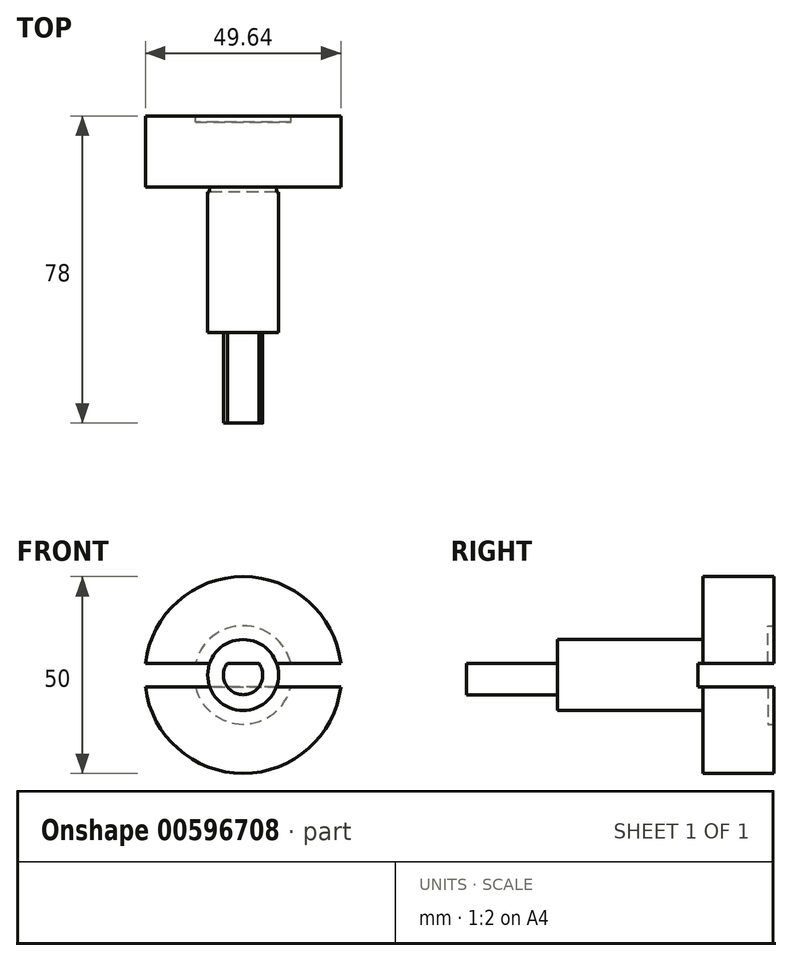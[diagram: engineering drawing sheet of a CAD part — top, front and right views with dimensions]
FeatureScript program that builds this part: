
annotation { "Feature Type Name" : "Feature", "Feature Type Description" : "" }
export const myFeature = defineFeature(function(context is Context, id is Id, definition is map)
    precondition{}
    {
        {
            var Q0;
            Q0=qCreatedBy(makeId("Right.planeOp"),FACE);
            var sketch = newSketch(context, id + "F0", { "sketchPlane" : qUnion([Q0])});
            skLineSegment(sketch, "E0", {"start": v(30.94, 0) * mm, "end": v(-47.06, 0) * mm});
            skLineSegment(sketch, "E1", {"start": v(-47.06, 0) * mm, "end": v(-47.06, -5) * mm});
            skLineSegment(sketch, "E2", {"start": v(-47.06, -5) * mm, "end": v(-24.06, -5) * mm});
            skLineSegment(sketch, "E3", {"start": v(-24.06, -5) * mm, "end": v(-24.06, -9) * mm});
            skLineSegment(sketch, "E4", {"start": v(-24.06, -9) * mm, "end": v(12.94, -9) * mm});
            skLineSegment(sketch, "E5", {"start": v(12.94, -9) * mm, "end": v(12.94, -25) * mm});
            skLineSegment(sketch, "E6", {"start": v(12.94, -25) * mm, "end": v(30.94, -25) * mm});
            skLineSegment(sketch, "E7", {"start": v(30.94, -25) * mm, "end": v(30.94, 0) * mm});
            skPoint(sketch, "E8.orphan", {"position": v(42.43, 0) * mm});
            skSolve(sketch);
        }
        {
            var Q0;
            Q0=makeQuery(id+"F0.imprint","IMPRINT",FACE,{"disambiguationData":[TD([[makeQuery(id+"F0.imprint","IMPRINT",EDGE,{"derivedFrom":sQuery(id+"F0.wireOp",EDGE,"E0")}),1.0]])]});
            var Q1;
            Q1=sQuery(id+"F0.wireOp",EDGE,"E0");
            revolve(context, id + "F1", {"entities" : qUnion([Q0]), "axis" : qUnion([Q1]), "revolveType" : RevolveType.FULL});
        }
        {
            var Q0;
            Q0=makeQuery(id+"F1.opRevolve","SWEPT_FACE",FACE,{"disambiguationData":[OSD([sQuery(id+"F0.wireOp",EDGE,"E1")])]});
            var sketch = newSketch(context, id + "F2", { "sketchPlane" : qUnion([Q0])});
            skLineSegment(sketch, "E9.bottom", {"start": v(-16.56, 13.75) * mm, "end": v(16.21, 13.75) * mm});
            skLineSegment(sketch, "E9.top", {"start": v(-16.56, 3) * mm, "end": v(16.21, 3) * mm});
            skLineSegment(sketch, "E9.left", {"start": v(-16.56, 13.75) * mm, "end": v(-16.56, 3) * mm});
            skLineSegment(sketch, "E9.right", {"start": v(16.21, 13.75) * mm, "end": v(16.21, 3) * mm});
            skSolve(sketch);
        }
        {
            var Q0;
            Q0 = qSketchRegion(id + "F2", true);
            var Q1;
            Q1=makeQuery(id+"F1.opRevolve","SWEPT_FACE",FACE,{"disambiguationData":[OSD([sQuery(id+"F0.wireOp",EDGE,"E3")])]});
            extrude(context, id + "F3", {"entities" : qUnion([Q0]), "operationType" : NewBodyOperationType.REMOVE, "endBound" : BoundingType.UP_TO_SURFACE, "oppositeDirection" : true, "depth" : 25 * mm, "endBoundEntityFace" : qUnion([Q1]), "offsetDistance" : 25 * mm});
        }
        {
            var Q0;
            Q0=makeQuery(id+"F1.opRevolve","SWEPT_FACE",FACE,{"disambiguationData":[OSD([sQuery(id+"F0.wireOp",EDGE,"E7")])]});
            var sketch = newSketch(context, id + "F4", { "sketchPlane" : qUnion([Q0])});
            skLineSegment(sketch, "E10.bottom", {"start": v(-27.5, 3) * mm, "end": v(27.5, 3) * mm});
            skLineSegment(sketch, "E10.top", {"start": v(-27.5, -3) * mm, "end": v(27.5, -3) * mm});
            skLineSegment(sketch, "E10.left", {"start": v(-27.5, 3) * mm, "end": v(-27.5, -3) * mm});
            skLineSegment(sketch, "E10.right", {"start": v(27.5, 3) * mm, "end": v(27.5, -3) * mm});
            skSolve(sketch);
        }
        {
            var Q0;
            Q0 = qSketchRegion(id + "F4", true);
            extrude(context, id + "F5", {"entities" : qUnion([Q0]), "operationType" : NewBodyOperationType.REMOVE, "oppositeDirection" : true, "depth" : 19.3 * mm, "offsetDistance" : 25 * mm});
        }
        {
            var Q0;
            Q0=makeQuery(id+"F5.boolean.opBoolean","SPLIT",FACE,{"disambiguationData":[TD([makeQuery(id+"F5.opExtrude","SWEPT_FACE",FACE,{"disambiguationData":[OSD([sQuery(id+"F4.wireOp",EDGE,"E10.bottom")])]})])],"derivedFrom":makeQuery(id+"F1.opRevolve","SWEPT_FACE",FACE,{"disambiguationData":[OSD([sQuery(id+"F0.wireOp",EDGE,"E7")])]})});
            var sketch = newSketch(context, id + "F6", { "sketchPlane" : qUnion([Q0])});
            skCircle(sketch, "E11", {"center": v(0, 0) * mm, "radius": 12.5 * mm});
            skSolve(sketch);
        }
        {
            var Q0;
            Q0 = qSketchRegion(id + "F6", true);
            extrude(context, id + "F7", {"entities" : qUnion([Q0]), "operationType" : NewBodyOperationType.REMOVE, "oppositeDirection" : true, "depth" : 1.5 * mm, "offsetDistance" : 25 * mm});
        }
    });
